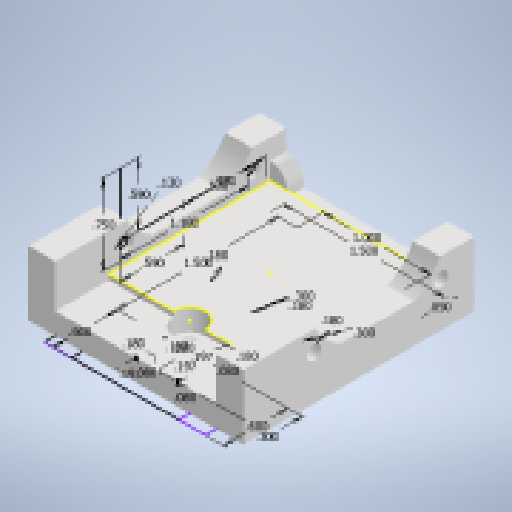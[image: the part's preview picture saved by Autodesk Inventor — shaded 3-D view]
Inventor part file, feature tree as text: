
AUTODESK INVENTOR PART (.ipt)
format: ipt  version: 2025.2 (Build 292293000, 293)  size: 529,920 bytes
history: native  units: in
note: dims shown in document units (in); Inventor stores cm internally (conversion verified against a paired STEP export)
features: sketch x15, extrude x13, thicken_offset x6, move_body x5, direct_edit x4, projected_geometry x2
ambient origin geometry x8: Origin, YZ Plane, XZ Plane, XY Plane, X Axis, Y Axis, Z Axis, Center Point
bodies: Solid1 (feature_tree)
feature tree (45):
  sketch  "Sketch1"  dims[d0=1.5in d1=1.0in]
  extrude  "Extrusion1"  Depth=1.5in
  extrude  "Extrusion2"  Depth=0.6in
  extrude  "Extrusion3"  Depth=1.5in
  extrude  "Extrusion4"  Depth=0.18in
  sketch  "Sketch3"  dims[d4=1.5in d5=0.18in]
  extrude  "Extrusion5"  Depth=0.05in
  sketch  "Sketch4"  dims[d6=0.18in d7=0.18in]
  extrude  "Extrusion6"  Depth=0.6in
  extrude  "Extrusion7"  Depth=0.3in
  extrude  "Extrusion8"  Depth=0.2in TaperAngle=0.0deg
  extrude  "Extrusion9"  Depth=0.2in TaperAngle=0.0deg
  thicken_offset  "Thicken1"
  thicken_offset  "Thicken2"
  thicken_offset  "Thicken3"
  thicken_offset  "Thicken4"
  thicken_offset  "Thicken5"
  thicken_offset  "Thicken6"
  extrude  "Extrusion10"  Depth=0.197in
  sketch  "Sketch10"  dims[d22=0.197in d23=0.197in]
  direct_edit  "Direct Edit1"
  sketch  "Sketch11"  dims[d24=0.08in d25=0.08in]
  extrude  "Extrusion11"  Depth=0.08in
  direct_edit  "Direct Edit2"
  extrude  "Extrusion12"  Depth=0.175in
  extrude  "Extrusion13"  Depth=0.4in
  direct_edit  "Direct Edit3"
  direct_edit  "Direct Edit4"
  sketch  "Sketch15"  dims[d33=1.0in d34=0.0in d35=0.05in d36=0.05in d37=1.55in d38=0.6in d39=0.0in d40=0.75in d41=0.59in d42=0.75in d43=0.59in d44=0.13in d45=1.18in d46=0.13in d47=2.0in d48=0.0in d49=0.25in d50=0.25in d51=2.0in d52=0.0in d53=0.2in d54=0.1in d55=0.2in d56=0.2in d57=0.3in d58=0.2in d59=0.3in d60=0.2in d61=0.1in d62=0.1in d63=0.2in d64=0.2in d66=1.75in d67=0.0in d68=0.0in d69=0.0in d70=-0.05in d71=0.0in d72=0.0in d73=-0.05in d74=0.197in d75=0.197in d76=0.08in d77=0.08in d78=0.16in d79=0.16in d80=0.16in d81=0.16in d82=0.16in d83=0.0in d84=0.0in d85=0.0in d86=-0.25in d87=0.24in d88=0.15in d89=0.5in d90=0.24in d91=0.5in d92=2.0in d93=0.0in d94=0.05in d95=0.0in d96=0.0in d97=0.0in d98=-0.01in d99=0.0in d100=0.0in d101=0.01in]
  sketch  "Sketch2"  dims[d2=0.18in d3=0.6in]
  sketch  "Sketch5"  dims[d8=0.25in d9=0.0in d10=0.05in]
  sketch  "Sketch6"  dims[d11=0.5in d12=0.0in d13=0.6in]
  sketch  "Sketch7"  dims[d14=0.3in d15=0.3in]
  sketch  "Sketch8"  dims[d16=0.3in d17=0.2in d18=0.0in]
  sketch  "Sketch9"  dims[d19=0.3in d20=0.2in d21=0.0in]
  sketch  "Sketch12"  dims[d26=0.175in d27=0.0in d28=0.18in]
  sketch  "Sketch13"  dims[d30=0.4in d31=0.4in]
  sketch  "Sketch14"  dims[d32=0.25in]
  projected_geometry  "Projected Loop1"
  projected_geometry  "Projected Loop2"
  move_body  "Move1"
  move_body  "Move2"
  move_body  "Move3"
  move_body  "Move4"
  move_body  "Move5"
